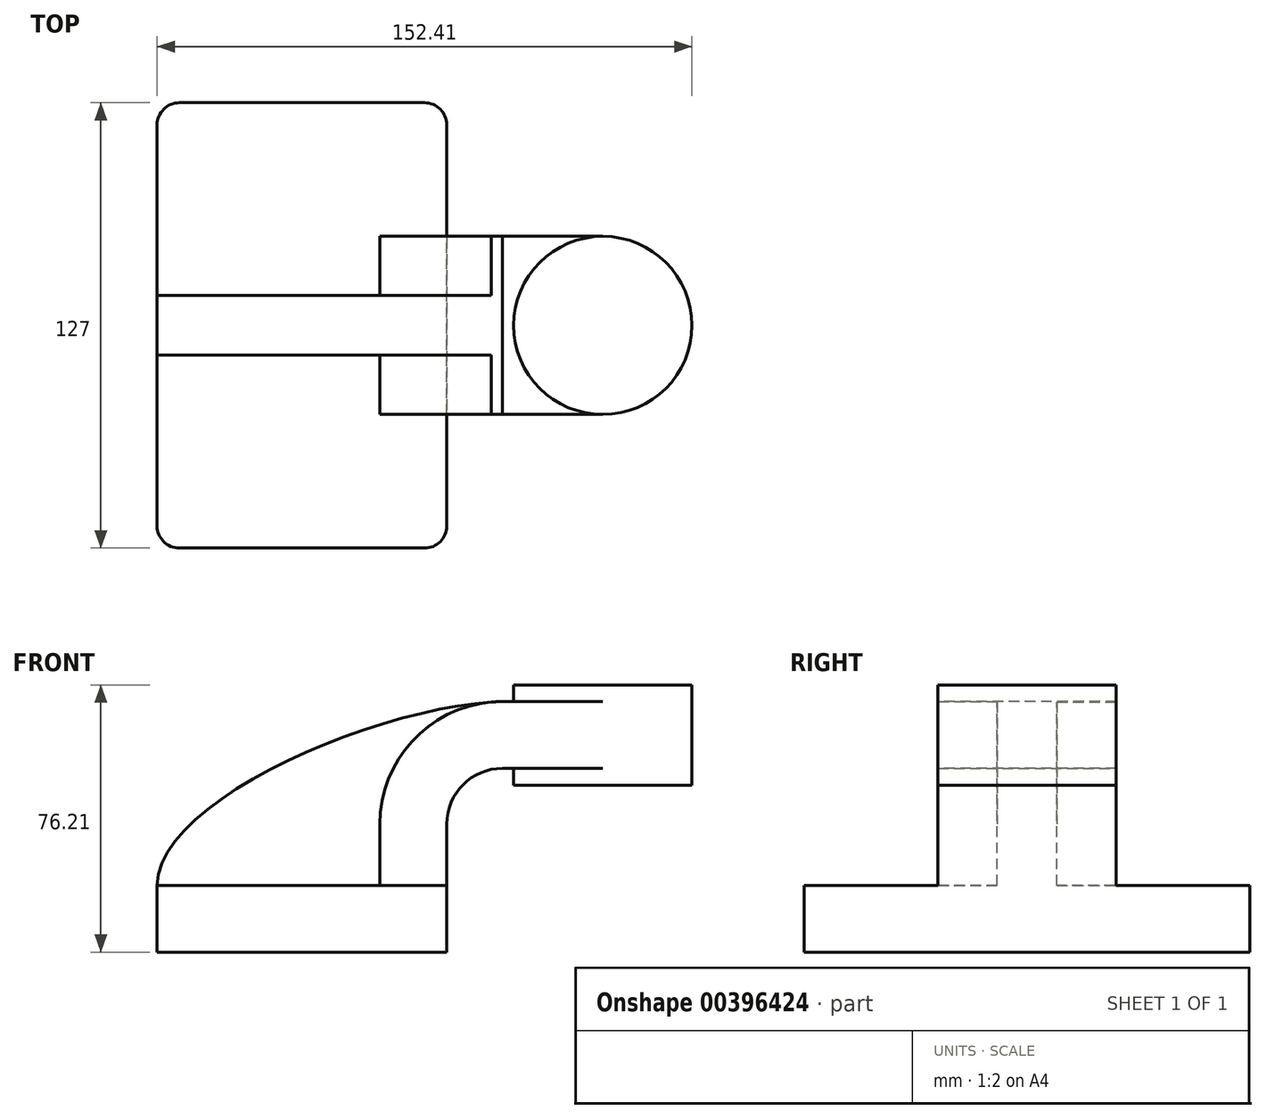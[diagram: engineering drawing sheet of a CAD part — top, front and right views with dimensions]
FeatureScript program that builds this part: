
annotation { "Feature Type Name" : "Feature", "Feature Type Description" : "" }
export const myFeature = defineFeature(function(context is Context, id is Id, definition is map)
    precondition{}
    {
        {
            var Q0;
            Q0=qCreatedBy(makeId("Front.planeOp"),FACE);
            var sketch = newSketch(context, id + "F0", { "sketchPlane" : qUnion([Q0])});
            skLineSegment(sketch, "E0.bottom", {"start": v(-41.28, 9.52) * mm, "end": v(41.27, 9.53) * mm});
            skLineSegment(sketch, "E0.top", {"start": v(-41.28, -9.53) * mm, "end": v(41.28, -9.53) * mm});
            skLineSegment(sketch, "E0.left", {"start": v(-41.28, 9.52) * mm, "end": v(-41.28, -9.53) * mm});
            skLineSegment(sketch, "E0.right", {"start": v(41.27, 9.53) * mm, "end": v(41.28, -9.52) * mm});
            skPoint(sketch, "E0.middle", {"position": v(0, 0) * mm});
            skLineSegment(sketch, "E1.bottom", {"start": v(60.32, 66.68) * mm, "end": v(111.12, 66.68) * mm});
            skLineSegment(sketch, "E1.top", {"start": v(60.32, 38.1) * mm, "end": v(111.12, 38.1) * mm});
            skLineSegment(sketch, "E1.left", {"start": v(60.32, 66.67) * mm, "end": v(60.32, 38.1) * mm});
            skLineSegment(sketch, "E1.right", {"start": v(111.12, 66.68) * mm, "end": v(111.12, 38.1) * mm});
            skPoint(sketch, "E1.middle", {"position": v(85.72, 52.39) * mm});
            skLineSegment(sketch, "E2", {"start": v(41.27, 9.53) * mm, "end": v(41.27, 27) * mm});
            skArc(sketch, "E3", {"start": v(41.27, 27) * mm, "mid": v(45.92, 38.23) * mm, "end": v(57.15, 42.88) * mm});
            skLineSegment(sketch, "E4", {"start": v(57.15, 42.88) * mm, "end": v(76.15, 42.88) * mm});
            skLineSegment(sketch, "E5.0", {"start": v(57.15, 61.93) * mm, "end": v(76.15, 61.93) * mm});
            skArc(sketch, "E5.1", {"start": v(22.22, 27) * mm, "mid": v(32.45, 51.7) * mm, "end": v(57.15, 61.93) * mm});
            skLineSegment(sketch, "E5.2", {"start": v(22.22, 9.53) * mm, "end": v(22.22, 27) * mm});
            skFitSpline(sketch, "E6", {"points": [v(-41.28, 9.52) * mm, v(57.15, 61.93) * mm], "startDerivative": vector(0, 73.9) * mm, "endDerivative": vector(102.17, 2.44) * mm});
            skLineSegment(sketch, "E7", {"start": v(76.15, 42.88) * mm, "end": v(85.72, 42.88) * mm});
            skLineSegment(sketch, "E8", {"start": v(85.72, 61.93) * mm, "end": v(76.15, 61.93) * mm});
            skLineSegment(sketch, "E9", {"start": v(85.72, 61.93) * mm, "end": v(85.72, 66.68) * mm});
            skLineSegment(sketch, "E10", {"start": v(85.72, 66.68) * mm, "end": v(85.72, 38.1) * mm});
            skSolve(sketch);
        }
        {
            var Q0;
            Q0=makeQuery(id+"F0.imprint","IMPRINT",FACE,{"disambiguationData":[TD([[makeQuery(id+"F0.imprint","IMPRINT",EDGE,{"derivedFrom":sQuery(id+"F0.wireOp",EDGE,"E0.top")}),1.0]])]});
            extrude(context, id + "F1", {"entities" : qUnion([Q0]), "endBound" : BoundingType.SYMMETRIC, "oppositeDirection" : true, "depth" : 127 * mm});
        }
        {
            var Q0;
            {var subQ1=sQuery(id+"F0.wireOp",EDGE,"E2");Q0=makeQuery(id+"F0.imprint","IMPRINT",FACE,{"disambiguationData":[TD([[makeQuery(id+"F0.imprint","IMPRINT",EDGE,{"derivedFrom":subQ1}),1.0]])]});}
            extrude(context, id + "F2", {"entities" : qUnion([Q0]), "operationType" : NewBodyOperationType.ADD, "endBound" : BoundingType.SYMMETRIC, "depth" : 50.8 * mm});
        }
        {
            var Q0;
            {var subQ3=sQuery(id+"F0.wireOp",EDGE,"E5.2");Q0=makeQuery(id+"F0.imprint","IMPRINT",FACE,{"disambiguationData":[TD([[makeQuery(id+"F0.imprint","IMPRINT",EDGE,{"derivedFrom":subQ3}),1.0]])]});}
            extrude(context, id + "F3", {"entities" : qUnion([Q0]), "operationType" : NewBodyOperationType.ADD, "endBound" : BoundingType.SYMMETRIC, "depth" : 17.02 * mm});
        }
        {
            var Q0;
            {var subQ0=sQuery(id+"F0.wireOp",EDGE,"E7");Q0=makeQuery(id+"F0.imprint","IMPRINT",FACE,{"disambiguationData":[TD([[makeQuery(id+"F0.imprint","IMPRINT",EDGE,{"derivedFrom":subQ0}),1.0]])]});}
            extrude(context, id + "F4", {"entities" : qUnion([Q0]), "operationType" : NewBodyOperationType.ADD, "endBound" : BoundingType.SYMMETRIC, "depth" : 50.8 * mm});
        }
        {
            var Q0;
            {var subQ0=sQuery(id+"F0.wireOp",EDGE,"E1.right");Q0=makeQuery(id+"F0.imprint","IMPRINT",FACE,{"disambiguationData":[TD([[makeQuery(id+"F0.imprint","IMPRINT",EDGE,{"derivedFrom":subQ0}),-1.0]])]});}
            var Q1;
            Q1=sQuery(id+"F0.wireOp",EDGE,"E10");
            revolve(context, id + "F5", {"operationType" : NewBodyOperationType.ADD, "entities" : qUnion([Q0]), "axis" : qUnion([Q1]), "revolveType" : RevolveType.FULL});
        }
        {
            var Q0;
            Q0=makeQuery(id+"F1.opExtrude","CAP_EDGE",EDGE,{"disambiguationData":[OSD([sQuery(id+"F0.wireOp",EDGE,"E0.left")])],"isStart":true});
            var Q1;
            Q1=makeQuery(id+"F1.opExtrude","CAP_EDGE",EDGE,{"disambiguationData":[OSD([sQuery(id+"F0.wireOp",EDGE,"E0.right")])],"isStart":true});
            var Q2;
            Q2=makeQuery(id+"F1.opExtrude","CAP_EDGE",EDGE,{"disambiguationData":[OSD([sQuery(id+"F0.wireOp",EDGE,"E0.left")])],"isStart":false});
            var Q3;
            Q3=makeQuery(id+"F1.opExtrude","CAP_EDGE",EDGE,{"disambiguationData":[OSD([sQuery(id+"F0.wireOp",EDGE,"E0.right")])],"isStart":false});
            fillet(context, id + "F6", {"entities" : qUnion([Q0, Q1, Q2, Q3]), "radius" : 6.35 * mm, "tangentPropagation" : true, "allowEdgeOverflow" : false});
        }
    });
